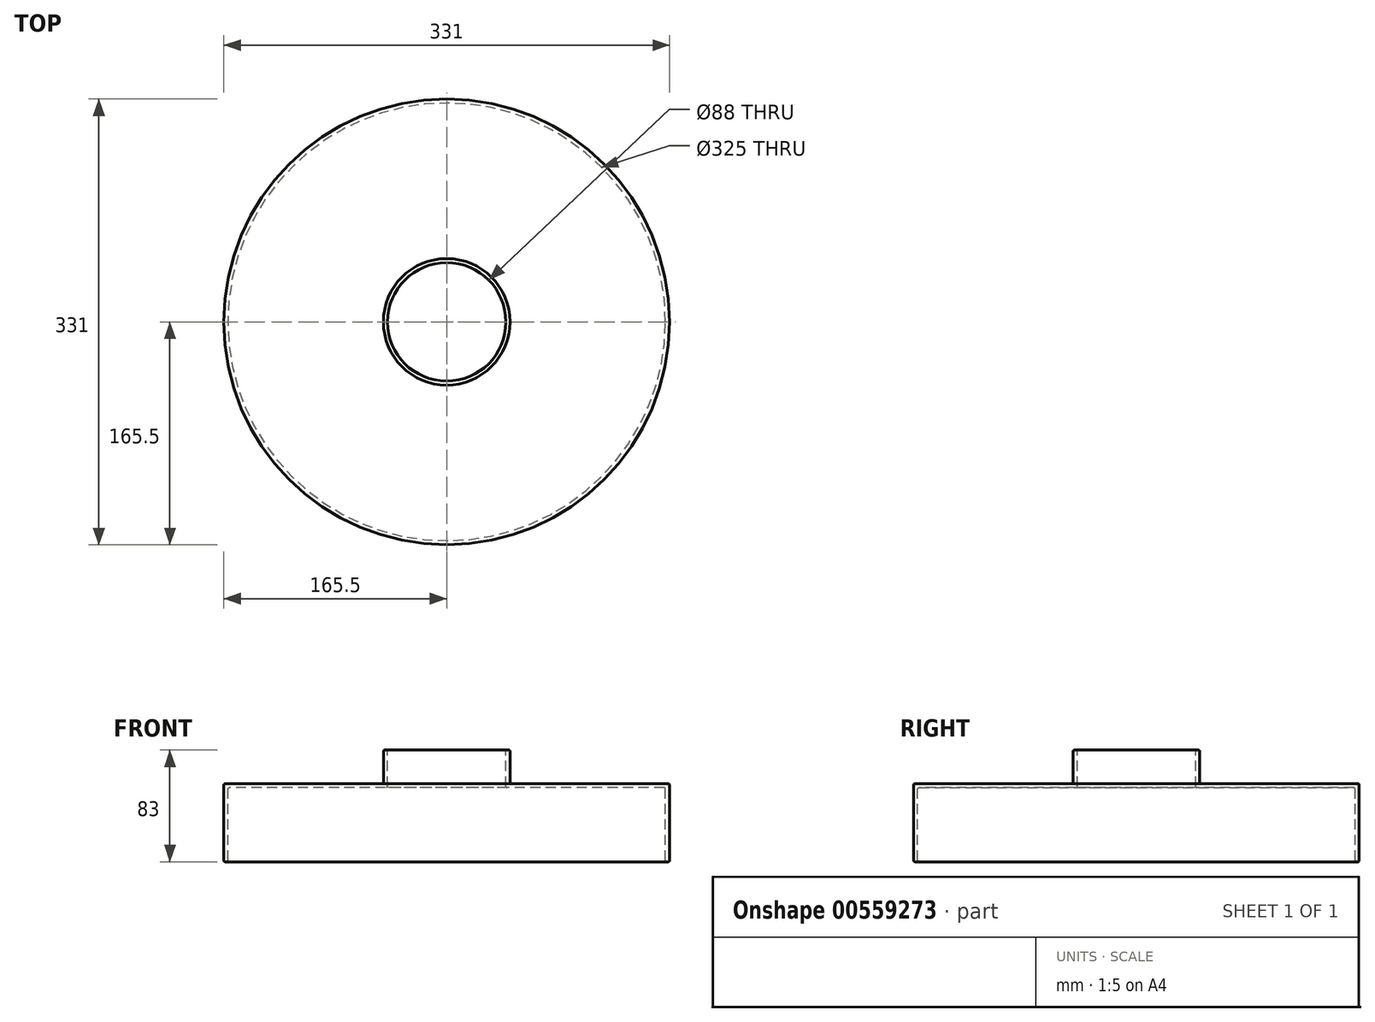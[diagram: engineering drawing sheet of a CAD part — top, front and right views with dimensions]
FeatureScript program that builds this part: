
annotation { "Feature Type Name" : "Feature", "Feature Type Description" : "" }
export const myFeature = defineFeature(function(context is Context, id is Id, definition is map)
    precondition{}
    {
        {
            var Q0;
            Q0=qCreatedBy(makeId("Right.planeOp"),FACE);
            var sketch = newSketch(context, id + "F0", { "sketchPlane" : qUnion([Q0])});
            skLineSegment(sketch, "E0.bottom", {"start": v(-161.5, 0) * mm, "end": v(-44, 0) * mm});
            skLineSegment(sketch, "E0.left", {"start": v(-162.5, -1) * mm, "end": v(-162.5, -54) * mm});
            skLineSegment(sketch, "E0.right", {"start": v(162.5, -1) * mm, "end": v(162.5, -54) * mm});
            skLineSegment(sketch, "E1.0", {"start": v(165.5, 2) * mm, "end": v(165.5, -54) * mm});
            skLineSegment(sketch, "E1.1", {"start": v(-164.5, 3) * mm, "end": v(-48, 3) * mm});
            skLineSegment(sketch, "E1.2", {"start": v(-165.5, 2) * mm, "end": v(-165.5, -54) * mm});
            skLineSegment(sketch, "E2", {"start": v(-164.5, -55) * mm, "end": v(-163.5, -55) * mm});
            skLineSegment(sketch, "E3", {"start": v(164.5, -55) * mm, "end": v(163.5, -55) * mm});
            skLineSegment(sketch, "E4", {"start": v(0, 57.77) * mm, "end": v(0, -99.22) * mm, "construction": true});
            skLineSegment(sketch, "E5", {"start": v(-44, 3) * mm, "end": v(-44, 1) * mm});
            skLineSegment(sketch, "E6", {"start": v(44, 0) * mm, "end": v(44, 3) * mm});
            skLineSegment(sketch, "E7.bottom", {"start": v(-45, 0) * mm, "end": v(-47, 0) * mm});
            skLineSegment(sketch, "E7.top", {"start": v(-45, 28) * mm, "end": v(-46, 28) * mm});
            skLineSegment(sketch, "E7.left", {"start": v(-44, 0) * mm, "end": v(-44, 27) * mm});
            skLineSegment(sketch, "E7.right", {"start": v(-47, 4) * mm, "end": v(-47, 27) * mm});
            skLineSegment(sketch, "E8.bottom", {"start": v(44, 0) * mm, "end": v(47, 0) * mm});
            skLineSegment(sketch, "E8.top", {"start": v(45, 28) * mm, "end": v(46, 28) * mm});
            skLineSegment(sketch, "E8.left", {"start": v(44, 1) * mm, "end": v(44, 27) * mm});
            skLineSegment(sketch, "E8.right", {"start": v(47, 4) * mm, "end": v(47, 27) * mm});
            skLineSegment(sketch, "E9.trimOffspring", {"start": v(48, 3) * mm, "end": v(164.5, 3) * mm});
            skLineSegment(sketch, "E10.trimOffspring", {"start": v(45, 0) * mm, "end": v(161.5, 0) * mm});
            skPoint(sketch, "E11.visualSharp", {"position": v(-47, 28) * mm});
            skArc(sketch, "E11.filletArc", {"start": v(-46, 28) * mm, "mid": v(-46.7, 27.7) * mm, "end": v(-47, 27) * mm});
            skPoint(sketch, "E12.visualSharp", {"position": v(-44, 28) * mm});
            skArc(sketch, "E12.filletArc", {"start": v(-44, 27) * mm, "mid": v(-44.3, 27.7) * mm, "end": v(-45, 28) * mm});
            skArc(sketch, "E13.filletArc", {"start": v(-48, 3) * mm, "mid": v(-47.3, 3.3) * mm, "end": v(-47, 4) * mm});
            skPoint(sketch, "E14.visualSharp", {"position": v(-44, 0) * mm});
            skArc(sketch, "E14.filletArc", {"start": v(-45, 0) * mm, "mid": v(-44.3, 0.3) * mm, "end": v(-44, 1) * mm});
            skPoint(sketch, "E15.visualSharp", {"position": v(-162.5, 0) * mm});
            skArc(sketch, "E15.filletArc", {"start": v(-161.5, 0) * mm, "mid": v(-162.2, -0.3) * mm, "end": v(-162.5, -1) * mm});
            skPoint(sketch, "E16.visualSharp", {"position": v(-165.5, 3) * mm});
            skArc(sketch, "E16.filletArc", {"start": v(-164.5, 3) * mm, "mid": v(-165.2, 2.7) * mm, "end": v(-165.5, 2) * mm});
            skPoint(sketch, "E17.visualSharp", {"position": v(-162.5, -55) * mm});
            skArc(sketch, "E17.filletArc", {"start": v(-163.5, -55) * mm, "mid": v(-162.8, -54.7) * mm, "end": v(-162.5, -54) * mm});
            skPoint(sketch, "E18.visualSharp", {"position": v(-165.5, -55) * mm});
            skArc(sketch, "E18.filletArc", {"start": v(-165.5, -54) * mm, "mid": v(-165.2, -54.7) * mm, "end": v(-164.5, -55) * mm});
            skPoint(sketch, "E19.visualSharp", {"position": v(47, 28) * mm});
            skArc(sketch, "E19.filletArc", {"start": v(47, 27) * mm, "mid": v(46.7, 27.7) * mm, "end": v(46, 28) * mm});
            skPoint(sketch, "E20.visualSharp", {"position": v(44, 28) * mm});
            skArc(sketch, "E20.filletArc", {"start": v(45, 28) * mm, "mid": v(44.3, 27.7) * mm, "end": v(44, 27) * mm});
            skArc(sketch, "E21.filletArc", {"start": v(47, 4) * mm, "mid": v(47.3, 3.3) * mm, "end": v(48, 3) * mm});
            skPoint(sketch, "E22.visualSharp", {"position": v(44, 0) * mm});
            skArc(sketch, "E22.filletArc", {"start": v(44, 1) * mm, "mid": v(44.3, 0.3) * mm, "end": v(45, 0) * mm});
            skPoint(sketch, "E23.visualSharp", {"position": v(162.5, 0) * mm});
            skArc(sketch, "E23.filletArc", {"start": v(162.5, -1) * mm, "mid": v(162.2, -0.3) * mm, "end": v(161.5, 0) * mm});
            skPoint(sketch, "E24.visualSharp", {"position": v(165.5, 3) * mm});
            skArc(sketch, "E24.filletArc", {"start": v(165.5, 2) * mm, "mid": v(165.2, 2.7) * mm, "end": v(164.5, 3) * mm});
            skPoint(sketch, "E25.visualSharp", {"position": v(165.5, -55) * mm});
            skArc(sketch, "E25.filletArc", {"start": v(164.5, -55) * mm, "mid": v(165.2, -54.7) * mm, "end": v(165.5, -54) * mm});
            skPoint(sketch, "E26.visualSharp", {"position": v(162.5, -55) * mm});
            skArc(sketch, "E26.filletArc", {"start": v(162.5, -54) * mm, "mid": v(162.8, -54.7) * mm, "end": v(163.5, -55) * mm});
            skSolve(sketch);
        }
        {
            var Q0;
            Q0=makeQuery(id+"F0.imprint","IMPRINT",FACE,{"disambiguationData":[TD([[makeQuery(id+"F0.imprint","IMPRINT",EDGE,{"derivedFrom":sQuery(id+"F0.wireOp",EDGE,"E0.left")}),-1.0]])]});
            var Q1;
            Q1=sQuery(id+"F0.wireOp",EDGE,"E4");
            revolve(context, id + "F1", {"entities" : qUnion([Q0]), "axis" : qUnion([Q1]), "revolveType" : RevolveType.FULL});
        }
    });
